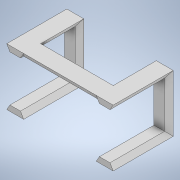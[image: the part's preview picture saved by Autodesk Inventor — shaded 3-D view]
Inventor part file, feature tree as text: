
AUTODESK INVENTOR PART (.ipt)
format: ipt  version: 2020 (Build 240168000, 168)  size: 175,104 bytes
history: native  units: mm
features: extrude x3, sketch x3
ambient origin geometry x8: Origin, YZ Plane, XZ Plane, XY Plane, X Axis, Y Axis, Z Axis, Center Point
bodies: Solid1 (feature_tree)
feature tree (6):
  extrude  "Extrusion1"  Depth=8.990381mm
  extrude  "Extrusion2"  Depth=32.412535mm
  extrude  "Extrusion3"  Depth=4.0mm
  sketch  "Sketch1"  dims[d0=118.0mm d1=8.990381mm]
  sketch  "Sketch2"  dims[d2=40.0mm d4=32.412535mm]
  sketch  "Sketch3"  dims[d5=10.0mm d7=10.0mm d9=4.0mm d10=2.0mm d11=2.0mm d12=4.0mm d13=41.309401mm d14=0.0mm d15=4.0mm d16=43.504809mm d17=0.0mm d18=7.650139mm d20=12.268941mm d21=12.268941mm d22=7.650139mm d23=38.547mm d24=0.0mm d25=0.5mm d26=0.872665mm d27=0.5mm d28=0.872665mm]
